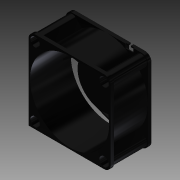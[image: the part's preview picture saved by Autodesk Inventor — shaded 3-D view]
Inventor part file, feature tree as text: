
AUTODESK INVENTOR PART (.ipt)
format: ipt  version: 2014 SP1 (Build 180222100, 222)  size: 282,624 bytes
history: native  units: mm (DEFAULTED — no unit token found)
features: sketch x10, extrude x9, plane x1, revolve x1, fillet x1, pattern_circular x1, other x1, projected_geometry x1
ambient origin geometry x8: Origin, YZ Plane, XZ Plane, XY Plane, X Axis, Y Axis, Z Axis, Center Point
bodies: Solid1 (feature_tree)
feature tree (25):
  extrude  "Extrusion1"  Depth=39.878mm
  plane  "Work Plane1"
  revolve  "Revolution1"  [1 undecoded]
  fillet  "Fillet1"  Radius=1.7018mm
  extrude  "Extrusion2"  TaperAngle=90.0deg  [1 undecoded]
  extrude  "Extrusion3"  Depth=3.175mm
  pattern_circular  "Circular Pattern1"  Count=4 Angle=360.0deg
  extrude  "Extrusion4"  Depth=19.812mm
  extrude  "fan support1"  Depth=0.635mm
  extrude  "fan support2"  Depth=3.81mm TaperAngle=0.0deg
  extrude  "fan support3"  Depth=8.001mm
  extrude  "fan support4"  Depth=1.5875mm
  extrude  "fan support5"  Depth=1.5875mm TaperAngle=0.0deg
  other  "fan interface"
  sketch  "Sketch1"  dims[d0=39.878mm d1=39.878mm]
  sketch  "Sketch2"  dims[d2=19.812mm d3=0.0mm d4=1.7018mm d5=1.7018mm]
  sketch  "Sketch3"  dims[d6=12.7mm d7=90.0deg]
  sketch  "Sketch4"  dims[d8=3.175mm d9=4.572mm]
  sketch  "Sketch5"  dims[d10=19.812mm d11=0.0mm]
  projected_geometry  "Projected Loop1"
  sketch  "Sketch6"  dims[d12=19.812mm d13=0.0mm d14=40.0mm d16=360.0deg]
  sketch  "Sketch7"  dims[d17=19.812mm d18=0.0mm d19=38.481mm]
  sketch  "Sketch8"  dims[d20=24.2824mm d21=0.635mm]
  sketch  "Sketch9"  dims[d23=0.635mm d24=3.81mm d25=0.0mm]
  sketch  "Sketch10"  dims[d26=5.08mm d27=8.001mm d28=4.0005mm d29=1.5875mm d30=0.0mm d31=22.896572mm d32=0.635mm d33=0.635mm d34=0.635mm d35=0.635mm d36=1.27mm d37=0.0mm d38=1.55575mm d39=0.0mm d40=1.55575mm d41=0.0mm d42=1.5875mm]
note: 2 required parameter values undecoded (feature->parameter linkage not recoverable at this tier; creation-order binding heuristic only, values carry confidence <= 0.55)